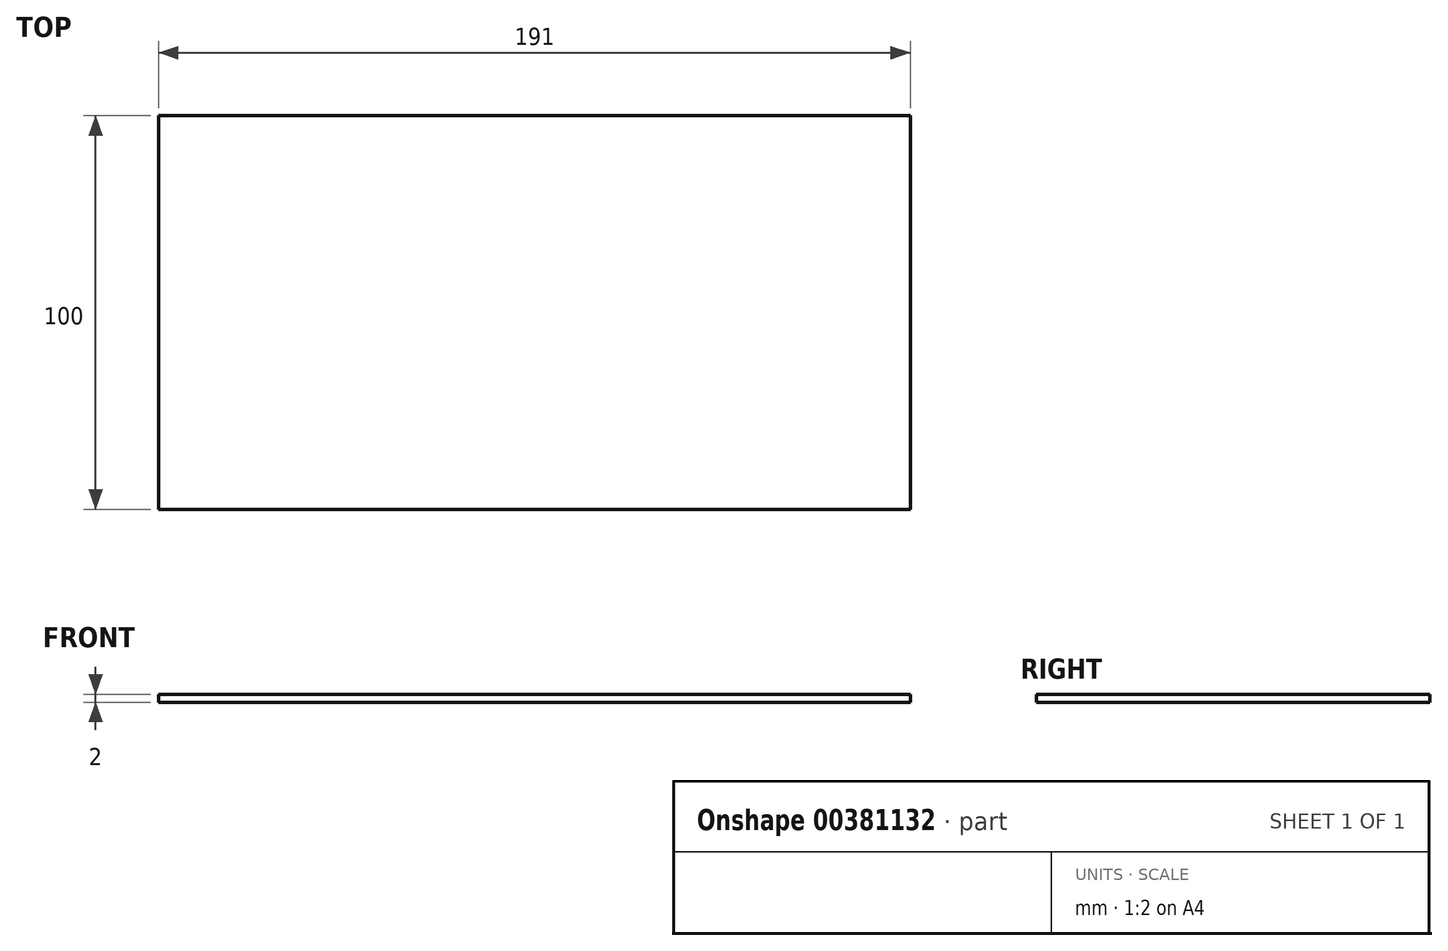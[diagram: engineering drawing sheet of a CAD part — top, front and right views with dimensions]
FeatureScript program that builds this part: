
annotation { "Feature Type Name" : "Feature", "Feature Type Description" : "" }
export const myFeature = defineFeature(function(context is Context, id is Id, definition is map)
    precondition{}
    {
        {
            var Q0;
            Q0=qCreatedBy(makeId("Top.planeOp"),FACE);
            var sketch = newSketch(context, id + "F0", { "sketchPlane" : qUnion([Q0])});
            skLineSegment(sketch, "E0.bottom", {"start": v(95.5, 50) * mm, "end": v(-95.5, 50) * mm});
            skLineSegment(sketch, "E0.top", {"start": v(95.5, -50) * mm, "end": v(-95.5, -50) * mm});
            skLineSegment(sketch, "E0.left", {"start": v(95.5, 50) * mm, "end": v(95.5, -50) * mm});
            skLineSegment(sketch, "E0.right", {"start": v(-95.5, 50) * mm, "end": v(-95.5, -50) * mm});
            skPoint(sketch, "E0.middle", {"position": v(0, 0) * mm});
            skSolve(sketch);
        }
        {
            var Q0;
            Q0 = qSketchRegion(id + "F0", true);
            extrude(context, id + "F1", {"entities" : qUnion([Q0]), "depth" : 2 * mm});
        }
    });
